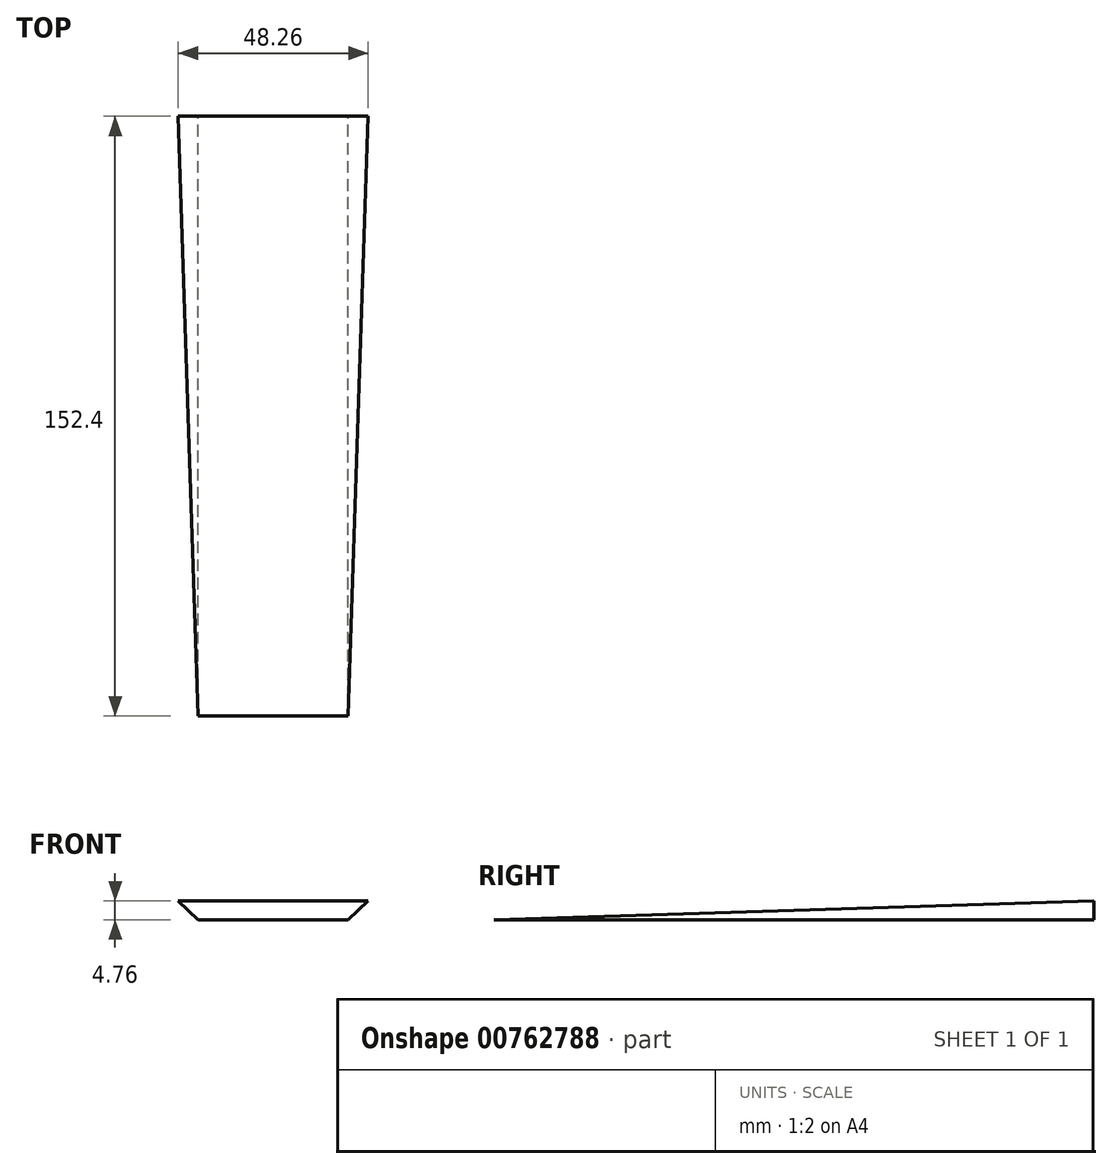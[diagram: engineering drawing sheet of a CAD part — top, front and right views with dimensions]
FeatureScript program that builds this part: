
annotation { "Feature Type Name" : "Feature", "Feature Type Description" : "" }
export const myFeature = defineFeature(function(context is Context, id is Id, definition is map)
    precondition{}
    {
        {
            var Q0;
            Q0=qCreatedBy(makeId("Front.planeOp"),FACE);
            var sketch = newSketch(context, id + "F0", { "sketchPlane" : qUnion([Q0])});
            skLineSegment(sketch, "E0.bottom", {"start": v(0, 0) * mm, "end": v(19.05, 0) * mm});
            skLineSegment(sketch, "E0.top", {"start": v(0, 4.76) * mm, "end": v(19.05, 4.76) * mm});
            skLineSegment(sketch, "E0.left", {"start": v(0, 0) * mm, "end": v(0, 4.76) * mm});
            skLineSegment(sketch, "E1", {"start": v(0, 21.75) * mm, "end": v(0, -18.45) * mm, "construction": true});
            skLineSegment(sketch, "E2", {"start": v(19.05, 4.76) * mm, "end": v(24.13, 4.76) * mm});
            skLineSegment(sketch, "E3", {"start": v(24.13, 4.76) * mm, "end": v(19.05, 0) * mm});
            skLineSegment(sketch, "E4.MirrorCS", {"start": v(0, 0) * mm, "end": v(-19.05, 0) * mm});
            skLineSegment(sketch, "E5.MirrorCS", {"start": v(0, 4.76) * mm, "end": v(-19.05, 4.76) * mm});
            skLineSegment(sketch, "E6.MirrorCS", {"start": v(-24.13, 4.76) * mm, "end": v(-19.05, 0) * mm});
            skLineSegment(sketch, "E7.MirrorCS", {"start": v(-19.05, 4.76) * mm, "end": v(-24.13, 4.76) * mm});
            skSolve(sketch);
        }
        {
            var Q0;
            Q0=makeQuery(id+"F0.imprint","IMPRINT",FACE,{"disambiguationData":[TD([[makeQuery(id+"F0.imprint","IMPRINT",EDGE,{"derivedFrom":sQuery(id+"F0.wireOp",EDGE,"E0.bottom")}),1.0]])]});
            var Q1;
            Q1=makeQuery(id+"F0.imprint","IMPRINT",FACE,{"disambiguationData":[TD([[makeQuery(id+"F0.imprint","IMPRINT",EDGE,{"derivedFrom":sQuery(id+"F0.wireOp",EDGE,"E4.MirrorCS")}),-1.0]])]});
            extrude(context, id + "F1", {"entities" : qUnion([Q0, Q1]), "depth" : 152.4 * mm, "offsetDistance" : 25.4 * mm});
        }
        {
            var Q0;
            Q0=qCreatedBy(makeId("Right.planeOp"),FACE);
            var sketch = newSketch(context, id + "F2", { "sketchPlane" : qUnion([Q0])});
            skLineSegment(sketch, "E8", {"start": v(0, 4.76) * mm, "end": v(-152.4, 0) * mm});
            skLineSegment(sketch, "E9", {"start": v(-152.4, 0) * mm, "end": v(-152.4, 4.76) * mm});
            skLineSegment(sketch, "E10", {"start": v(-152.4, 4.76) * mm, "end": v(0, 4.76) * mm});
            skSolve(sketch);
        }
        {
            var Q0;
            Q0 = qSketchRegion(id + "F2", true);
            extrude(context, id + "F3", {"entities" : qUnion([Q0]), "operationType" : NewBodyOperationType.REMOVE, "endBound" : BoundingType.SYMMETRIC, "oppositeDirection" : true, "depth" : 50.8 * mm, "offsetDistance" : 25.4 * mm});
        }
    });
